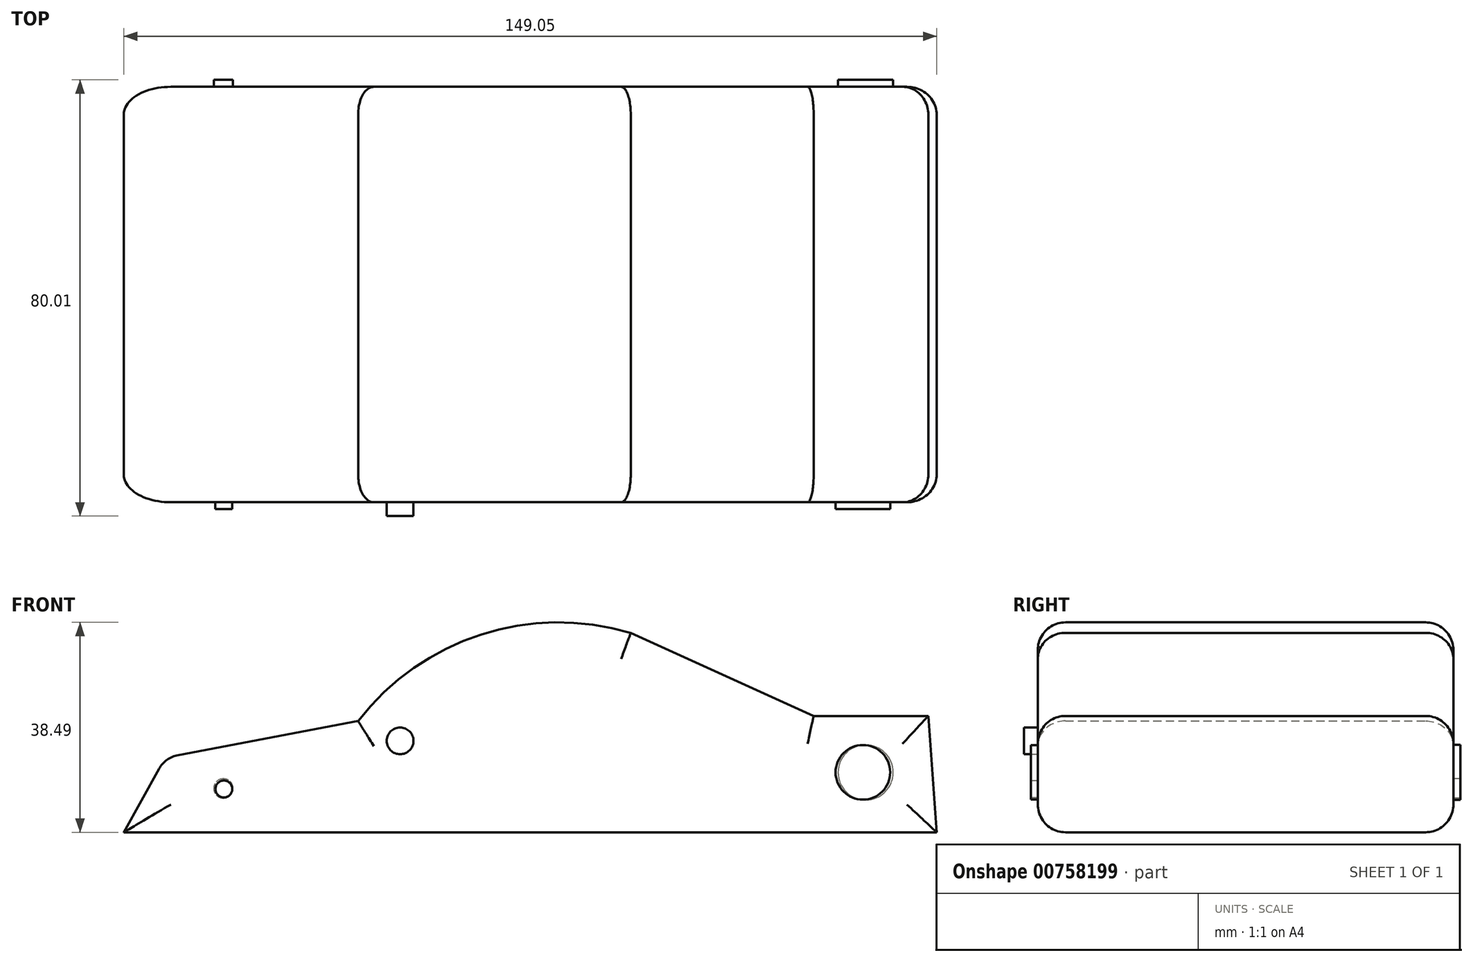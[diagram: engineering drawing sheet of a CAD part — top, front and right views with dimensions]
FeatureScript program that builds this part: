
annotation { "Feature Type Name" : "Feature", "Feature Type Description" : "" }
export const myFeature = defineFeature(function(context is Context, id is Id, definition is map)
    precondition{}
    {
        {
            var Q0;
            Q0=qCreatedBy(makeId("Front.planeOp"),FACE);
            var sketch = newSketch(context, id + "F0", { "sketchPlane" : qUnion([Q0])});
            skLineSegment(sketch, "E0", {"start": v(-72.09, 0) * mm, "end": v(76.96, 0) * mm});
            skLineSegment(sketch, "E1", {"start": v(-72.09, 0) * mm, "end": v(-64.47, 13.72) * mm});
            skLineSegment(sketch, "E2", {"start": v(-64.47, 13.72) * mm, "end": v(-29.1, 20.42) * mm});
            skArc(sketch, "E3", {"start": v(20.88, 36.58) * mm, "mid": v(-6.62, 36.24) * mm, "end": v(-29.1, 20.42) * mm});
            skLineSegment(sketch, "E4", {"start": v(20.88, 36.58) * mm, "end": v(54.4, 21.34) * mm});
            skLineSegment(sketch, "E5", {"start": v(54.4, 21.34) * mm, "end": v(75.44, 21.34) * mm});
            skLineSegment(sketch, "E6", {"start": v(75.44, 21.34) * mm, "end": v(76.96, 0) * mm});
            skSolve(sketch);
        }
        {
            var Q0;
            Q0=makeQuery(id+"F0.imprint","IMPRINT",FACE,{"disambiguationData":[TD([[makeQuery(id+"F0.imprint","IMPRINT",EDGE,{"derivedFrom":sQuery(id+"F0.wireOp",EDGE,"E0")}),1.0]])]});
            extrude(context, id + "F1", {"entities" : qUnion([Q0]), "depth" : 76.2 * mm, "offsetDistance" : 25.4 * mm});
        }
        {
            var Q0;
            Q0=makeQuery(id+"F1.opExtrude","CAP_EDGE",EDGE,{"disambiguationData":[OSD([sQuery(id+"F0.wireOp",EDGE,"E2")])],"isStart":false});
            var Q1;
            Q1=makeQuery(id+"F1.opExtrude","SWEPT_EDGE",EDGE,{"disambiguationData":[OSD([sQuery(id+"F0.wireOp",EDGE,"E1"),sQuery(id+"F0.wireOp",EDGE,"E2")])]});
            var Q2;
            Q2=makeQuery(id+"F1.opExtrude","CAP_EDGE",EDGE,{"disambiguationData":[OSD([sQuery(id+"F0.wireOp",EDGE,"E2")])],"isStart":true});
            var Q3;
            Q3=makeQuery(id+"F1.opExtrude","CAP_EDGE",EDGE,{"disambiguationData":[OSD([sQuery(id+"F0.wireOp",EDGE,"E1")])],"isStart":true});
            var Q4;
            Q4=makeQuery(id+"F1.opExtrude","CAP_EDGE",EDGE,{"disambiguationData":[OSD([sQuery(id+"F0.wireOp",EDGE,"E1")])],"isStart":false});
            var Q5;
            Q5=makeQuery(id+"F1.opExtrude","CAP_FACE",FACE,{"disambiguationData":[OSD([sQuery(id+"F0.wireOp",EDGE,"E0"),sQuery(id+"F0.wireOp",EDGE,"E1"),sQuery(id+"F0.wireOp",EDGE,"E2"),sQuery(id+"F0.wireOp",EDGE,"E3"),sQuery(id+"F0.wireOp",EDGE,"E4"),sQuery(id+"F0.wireOp",EDGE,"E5"),sQuery(id+"F0.wireOp",EDGE,"E6")])],"isStart":false});
            var Q6;
            Q6=makeQuery(id+"F1.opExtrude","CAP_EDGE",EDGE,{"disambiguationData":[OSD([sQuery(id+"F0.wireOp",EDGE,"E0")])],"isStart":true});
            var Q7;
            Q7=makeQuery(id+"F1.opExtrude","CAP_FACE",FACE,{"disambiguationData":[OSD([sQuery(id+"F0.wireOp",EDGE,"E0"),sQuery(id+"F0.wireOp",EDGE,"E1"),sQuery(id+"F0.wireOp",EDGE,"E2"),sQuery(id+"F0.wireOp",EDGE,"E3"),sQuery(id+"F0.wireOp",EDGE,"E4"),sQuery(id+"F0.wireOp",EDGE,"E5"),sQuery(id+"F0.wireOp",EDGE,"E6")])],"isStart":true});
            fillet(context, id + "F2", {"entities" : qUnion([Q0, Q1, Q2, Q3, Q4, Q5, Q6, Q7]), "radius" : 5.08 * mm, "tangentPropagation" : true, "allowEdgeOverflow" : false});
        }
        {
            var Q0;
            Q0=makeQuery(id+"F1.opExtrude","CAP_FACE",FACE,{"disambiguationData":[OSD([sQuery(id+"F0.wireOp",EDGE,"E0"),sQuery(id+"F0.wireOp",EDGE,"E1"),sQuery(id+"F0.wireOp",EDGE,"E2"),sQuery(id+"F0.wireOp",EDGE,"E3"),sQuery(id+"F0.wireOp",EDGE,"E4"),sQuery(id+"F0.wireOp",EDGE,"E5"),sQuery(id+"F0.wireOp",EDGE,"E6")])],"isStart":true});
            var sketch = newSketch(context, id + "F3", { "sketchPlane" : qUnion([Q0])});
            skCircle(sketch, "E7", {"center": v(-63.93, 10.97) * mm, "radius": 5.05 * mm});
            skSolve(sketch);
        }
        {
            var Q0;
            Q0 = qSketchRegion(id + "F3", true);
            extrude(context, id + "F4", {"entities" : qUnion([Q0]), "operationType" : NewBodyOperationType.ADD, "depth" : 1.27 * mm, "offsetDistance" : 25.4 * mm});
        }
        {
            var Q0;
            Q0=makeQuery(id+"F1.opExtrude","CAP_FACE",FACE,{"disambiguationData":[OSD([sQuery(id+"F0.wireOp",EDGE,"E0"),sQuery(id+"F0.wireOp",EDGE,"E1"),sQuery(id+"F0.wireOp",EDGE,"E2"),sQuery(id+"F0.wireOp",EDGE,"E3"),sQuery(id+"F0.wireOp",EDGE,"E4"),sQuery(id+"F0.wireOp",EDGE,"E5"),sQuery(id+"F0.wireOp",EDGE,"E6")])],"isStart":false});
            var sketch = newSketch(context, id + "F5", { "sketchPlane" : qUnion([Q0])});
            skCircle(sketch, "E8", {"center": v(63.44, 11) * mm, "radius": 5 * mm});
            skSolve(sketch);
        }
        {
            var Q0;
            Q0=makeQuery(id+"F5.imprint","IMPRINT",FACE,{"disambiguationData":[TD([[makeQuery(id+"F5.imprint","IMPRINT",EDGE,{"derivedFrom":sQuery(id+"F5.wireOp",EDGE,"E8")}),1.0]])]});
            extrude(context, id + "F6", {"entities" : qUnion([Q0]), "operationType" : NewBodyOperationType.ADD, "depth" : 1.27 * mm, "offsetDistance" : 25.4 * mm});
        }
        {
            var Q0;
            Q0=makeQuery(id+"F1.opExtrude","CAP_FACE",FACE,{"disambiguationData":[OSD([sQuery(id+"F0.wireOp",EDGE,"E0"),sQuery(id+"F0.wireOp",EDGE,"E1"),sQuery(id+"F0.wireOp",EDGE,"E2"),sQuery(id+"F0.wireOp",EDGE,"E3"),sQuery(id+"F0.wireOp",EDGE,"E4"),sQuery(id+"F0.wireOp",EDGE,"E5"),sQuery(id+"F0.wireOp",EDGE,"E6")])],"isStart":false});
            var sketch = newSketch(context, id + "F7", { "sketchPlane" : qUnion([Q0])});
            skCircle(sketch, "E9", {"center": v(-53.72, 7.92) * mm, "radius": 1.55 * mm});
            skSolve(sketch);
        }
        {
            var Q0;
            Q0=makeQuery(id+"F7.imprint","IMPRINT",FACE,{"disambiguationData":[TD([[makeQuery(id+"F7.imprint","IMPRINT",EDGE,{"derivedFrom":sQuery(id+"F7.wireOp",EDGE,"E9")}),1.0]])]});
            extrude(context, id + "F8", {"entities" : qUnion([Q0]), "operationType" : NewBodyOperationType.ADD, "depth" : 1.27 * mm, "offsetDistance" : 25.4 * mm});
        }
        {
            var Q0;
            Q0=makeQuery(id+"F1.opExtrude","CAP_FACE",FACE,{"disambiguationData":[OSD([sQuery(id+"F0.wireOp",EDGE,"E0"),sQuery(id+"F0.wireOp",EDGE,"E1"),sQuery(id+"F0.wireOp",EDGE,"E2"),sQuery(id+"F0.wireOp",EDGE,"E3"),sQuery(id+"F0.wireOp",EDGE,"E4"),sQuery(id+"F0.wireOp",EDGE,"E5"),sQuery(id+"F0.wireOp",EDGE,"E6")])],"isStart":true});
            var sketch = newSketch(context, id + "F9", { "sketchPlane" : qUnion([Q0])});
            skCircle(sketch, "E10", {"center": v(53.81, 8.04) * mm, "radius": 1.77 * mm});
            skSolve(sketch);
        }
        {
            var Q0;
            Q0=makeQuery(id+"F9.imprint","IMPRINT",FACE,{"disambiguationData":[TD([[makeQuery(id+"F9.imprint","IMPRINT",EDGE,{"derivedFrom":sQuery(id+"F9.wireOp",EDGE,"E10")}),1.0]])]});
            extrude(context, id + "F10", {"entities" : qUnion([Q0]), "operationType" : NewBodyOperationType.ADD, "depth" : 1.27 * mm, "offsetDistance" : 25.4 * mm});
        }
        {
            var Q0;
            Q0=makeQuery(id+"F7.imprint","IMPRINT",FACE,{"disambiguationData":[TD([[makeQuery(id+"F7.imprint","IMPRINT",EDGE,{"derivedFrom":sQuery(id+"F7.wireOp",EDGE,"E9")}),-1.0]])]});
            var sketch = newSketch(context, id + "F11", { "sketchPlane" : qUnion([Q0])});
            skCircle(sketch, "E11", {"center": v(-21.41, 16.76) * mm, "radius": 2.46 * mm});
            skSolve(sketch);
        }
        {
            var Q0;
            Q0 = qSketchRegion(id + "F11", true);
            extrude(context, id + "F12", {"entities" : qUnion([Q0]), "operationType" : NewBodyOperationType.ADD, "depth" : 2.54 * mm, "offsetDistance" : 25.4 * mm});
        }
    });
